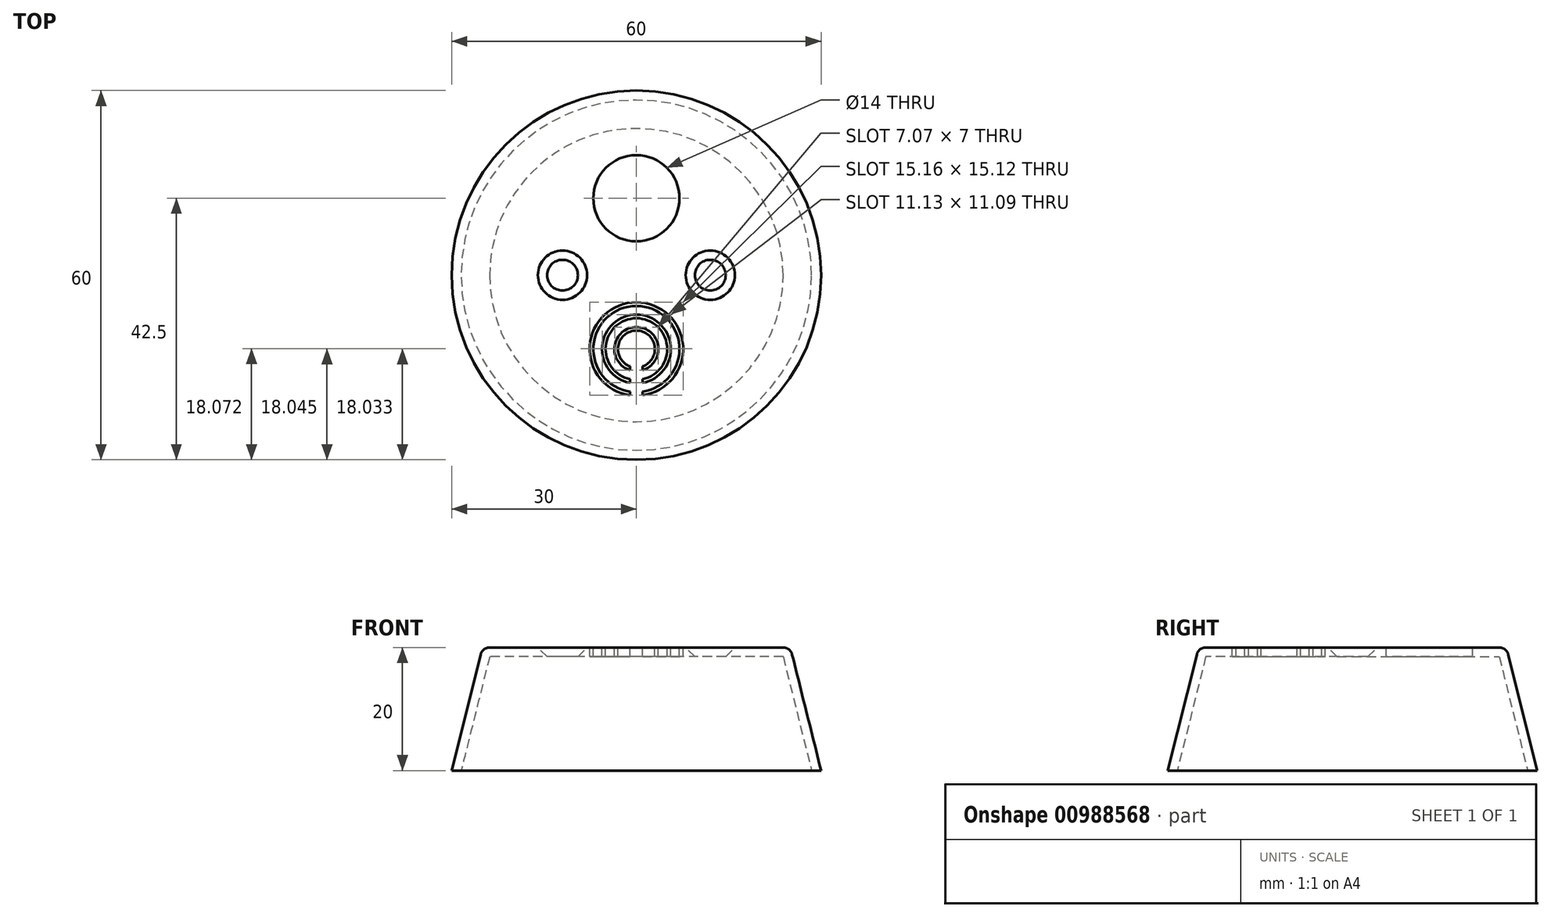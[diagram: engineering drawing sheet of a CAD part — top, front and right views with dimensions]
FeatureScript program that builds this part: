
annotation { "Feature Type Name" : "Feature", "Feature Type Description" : "" }
export const myFeature = defineFeature(function(context is Context, id is Id, definition is map)
    precondition{}
    {
        {
            var Q0;
            Q0=qCreatedBy(makeId("Front.planeOp"),FACE);
            var sketch = newSketch(context, id + "F0", { "sketchPlane" : qUnion([Q0])});
            skLineSegment(sketch, "E0", {"start": v(0, 20) * mm, "end": v(25, 20) * mm});
            skLineSegment(sketch, "E1", {"start": v(25, 20) * mm, "end": v(30, 0) * mm});
            skLineSegment(sketch, "E2", {"start": v(30, 0) * mm, "end": v(0, 0) * mm});
            skLineSegment(sketch, "E3", {"start": v(0, 0) * mm, "end": v(0, 20) * mm});
            skSolve(sketch);
        }
        {
            var Q0;
            Q0=qCreatedBy(makeId("Front.planeOp"),FACE);
            var sketch = newSketch(context, id + "F1", { "sketchPlane" : qUnion([Q0])});
            skLineSegment(sketch, "E4", {"start": v(0, 54.15) * mm, "end": v(0, -21.9) * mm});
            skSolve(sketch);
        }
        {
            var Q0;
            Q0=makeQuery(id+"F0.imprint","IMPRINT",FACE,{"disambiguationData":[TD([[makeQuery(id+"F0.imprint","IMPRINT",EDGE,{"derivedFrom":sQuery(id+"F0.wireOp",EDGE,"E0")}),-1.0]])]});
            var Q1;
            Q1=sQuery(id+"F1.wireOp",EDGE,"E4");
            revolve(context, id + "F2", {"surfaceOperationType" : NewSurfaceOperationType.NEW, "entities" : qUnion([Q0]), "axis" : qUnion([Q1]), "revolveType" : RevolveType.FULL});
        }
        {
            var Q0;
            Q0=makeQuery(id+"F2.opRevolve","SWEPT_EDGE",EDGE,{"disambiguationData":[OSD([sQuery(id+"F0.wireOp",EDGE,"E0"),sQuery(id+"F0.wireOp",EDGE,"E1")])]});
            fillet(context, id + "F3", {"entities" : qUnion([Q0]), "radius" : 1.5 * mm, "tangentPropagation" : true, "allowEdgeOverflow" : false});
        }
        {
            var Q0;
            Q0=makeQuery(id+"F2.opRevolve","SWEPT_FACE",FACE,{"disambiguationData":[OSD([sQuery(id+"F0.wireOp",EDGE,"E2")])]});
            shell(context, id + "F4", {"entities" : qUnion([Q0]), "thickness" : 1.5 * mm});
        }
        {
            var Q0;
            Q0=makeQuery(id+"F2.opRevolve","SWEPT_FACE",FACE,{"disambiguationData":[OSD([sQuery(id+"F0.wireOp",EDGE,"E0")])]});
            var sketch = newSketch(context, id + "F5", { "sketchPlane" : qUnion([Q0])});
            skCircle(sketch, "E5", {"center": v(0, 12.5) * mm, "radius": 7 * mm});
            skSolve(sketch);
        }
        {
            var Q0;
            Q0 = qSketchRegion(id + "F5", true);
            extrude(context, id + "F6", {"entities" : qUnion([Q0]), "operationType" : NewBodyOperationType.REMOVE, "endBound" : BoundingType.THROUGH_ALL, "oppositeDirection" : true, "depth" : 25 * mm, "offsetDistance" : 25 * mm});
        }
        {
            var Q0;
            Q0=makeQuery(id+"F2.opRevolve","SWEPT_FACE",FACE,{"disambiguationData":[OSD([sQuery(id+"F0.wireOp",EDGE,"E0")])]});
            var sketch = newSketch(context, id + "F7", { "sketchPlane" : qUnion([Q0])});
            skPoint(sketch, "E6", {"position": v(12, 0) * mm});
            skPoint(sketch, "E7.MirrorP", {"position": v(-12, 0) * mm});
            skSolve(sketch);
        }
        {
            var Q0;
            Q0=sQuery(id+"F7.wireOp",VERTEX,"E6");
            var Q1;
            Q1=sQuery(id+"F7.wireOp",VERTEX,"E7.MirrorP");
            var Q2;
            Q2=makeQuery(id+"F2.opRevolve","SWEPT_BODY",BODY,{"disambiguationData":[OSD([sQuery(id+"F0.wireOp",EDGE,"E0"),sQuery(id+"F0.wireOp",EDGE,"E1"),sQuery(id+"F0.wireOp",EDGE,"E2"),sQuery(id+"F0.wireOp",EDGE,"E3")])]});
            hole(context, id + "F8", {"style" : HoleStyle.C_SINK, "endStyle" : HoleEndStyle.THROUGH, "holeDiameter" : 4 * mm, "cSinkDiameter" : 8 * mm, "cSinkAngle" : 90 * degree, "majorDiameter" : 5 * mm, "isTappedThrough" : true, "tappedDepth" : 12 * mm, "tapClearance" : 3, "locations" : qUnion([Q0, Q1]), "scope" : qUnion([Q2]), "startStyle" : HoleStartStyle.SKETCH});
        }
        {
            var Q0;
            Q0=makeQuery(id+"F2.opRevolve","SWEPT_FACE",FACE,{"disambiguationData":[OSD([sQuery(id+"F0.wireOp",EDGE,"E0")])]});
            var sketch = newSketch(context, id + "F9", { "sketchPlane" : qUnion([Q0])});
            skArc(sketch, "E8", {"start": v(1, -14.83) * mm, "mid": v(0, -9) * mm, "end": v(-1, -14.83) * mm});
            skArc(sketch, "E9", {"start": v(1, -15.43) * mm, "mid": v(0, -8.43) * mm, "end": v(-1, -15.43) * mm});
            skLineSegment(sketch, "E10", {"start": v(1, -14.83) * mm, "end": v(1, -15.43) * mm});
            skLineSegment(sketch, "E11", {"start": v(-1, -14.83) * mm, "end": v(-1, -15.43) * mm});
            skArc(sketch, "E12", {"start": v(1, -16.9) * mm, "mid": v(0, -7) * mm, "end": v(-1, -16.9) * mm});
            skArc(sketch, "E13", {"start": v(1, -17.5) * mm, "mid": v(0, -6.41) * mm, "end": v(-1, -17.5) * mm});
            skLineSegment(sketch, "E14", {"start": v(1, -16.9) * mm, "end": v(1, -17.5) * mm});
            skLineSegment(sketch, "E15", {"start": v(-1, -16.9) * mm, "end": v(-1, -17.5) * mm});
            skArc(sketch, "E16", {"start": v(1, -18.93) * mm, "mid": v(0, -5) * mm, "end": v(-1, -18.93) * mm});
            skArc(sketch, "E17", {"start": v(1, -19.53) * mm, "mid": v(0, -4.4) * mm, "end": v(-1, -19.53) * mm});
            skLineSegment(sketch, "E18", {"start": v(1, -18.93) * mm, "end": v(1, -19.53) * mm});
            skLineSegment(sketch, "E19", {"start": v(-1, -18.93) * mm, "end": v(-1, -19.53) * mm});
            skSolve(sketch);
        }
        {
            var Q0;
            Q0 = qSketchRegion(id + "F9", true);
            extrude(context, id + "F10", {"entities" : qUnion([Q0]), "operationType" : NewBodyOperationType.REMOVE, "endBound" : BoundingType.THROUGH_ALL, "oppositeDirection" : true, "depth" : 25 * mm, "offsetDistance" : 25 * mm});
        }
    });
